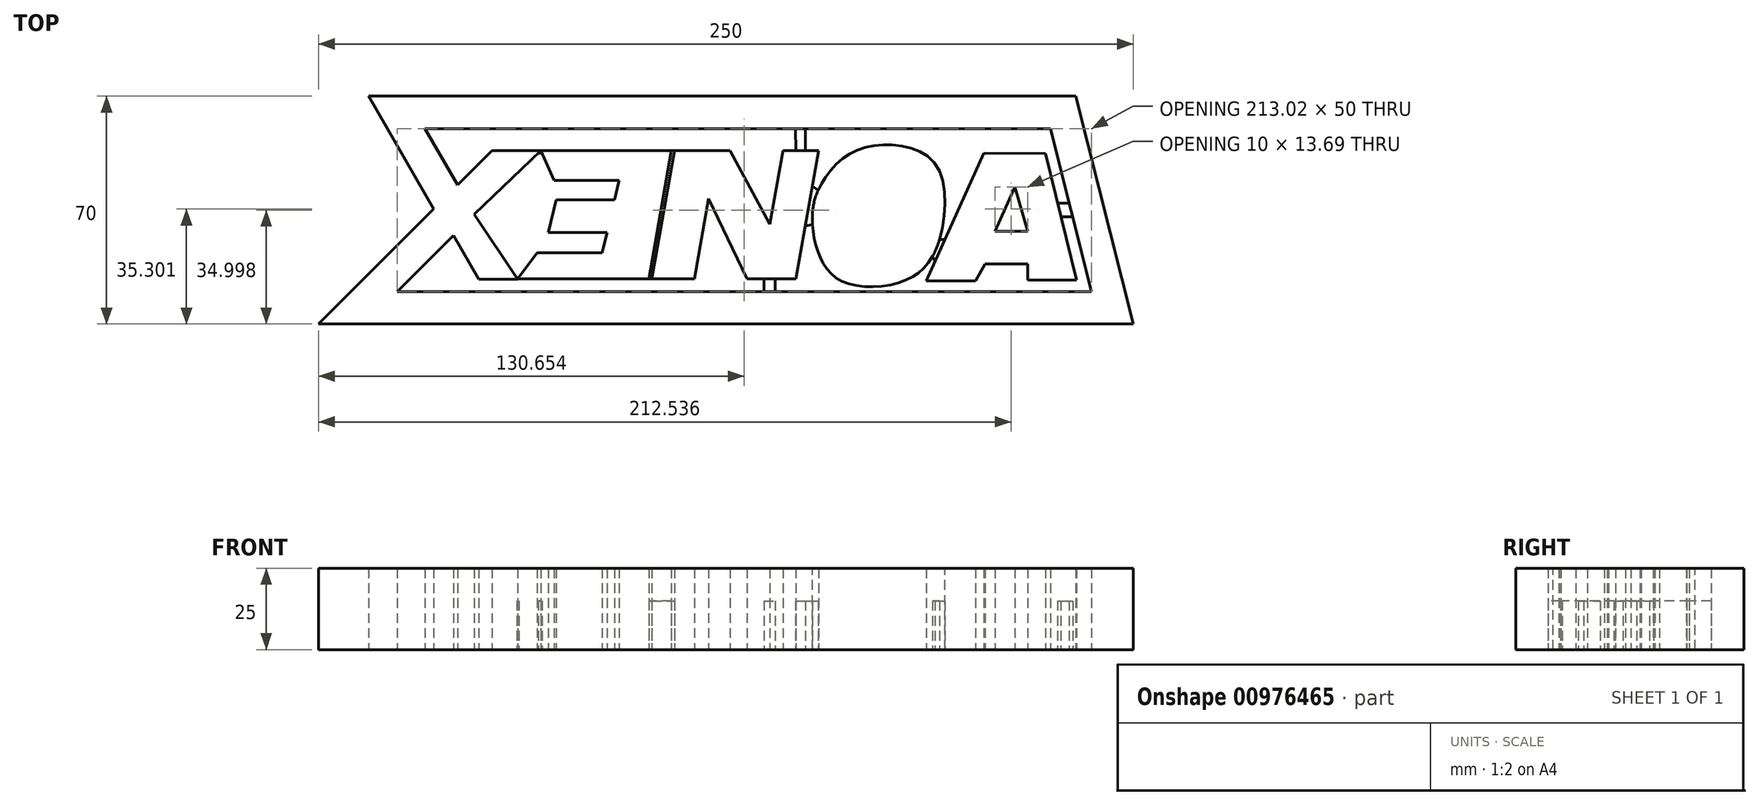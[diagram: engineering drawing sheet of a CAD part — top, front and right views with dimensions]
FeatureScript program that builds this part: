
annotation { "Feature Type Name" : "Feature", "Feature Type Description" : "" }
export const myFeature = defineFeature(function(context is Context, id is Id, definition is map)
    precondition{}
    {
        {
            var Q0;
            Q0=qCreatedBy(makeId("Top.planeOp"),FACE);
            var sketch = newSketch(context, id + "F0", { "sketchPlane" : qUnion([Q0])});
            skLineSegment(sketch, "E0", {"start": v(0, 0) * mm, "end": v(250, 0) * mm});
            skLineSegment(sketch, "E1", {"start": v(0, 0) * mm, "end": v(35.36, 35.36) * mm});
            skLineSegment(sketch, "E2", {"start": v(35.36, 35.36) * mm, "end": v(15.36, 70) * mm});
            skLineSegment(sketch, "E3", {"start": v(15.36, 70) * mm, "end": v(232.36, 70) * mm});
            skLineSegment(sketch, "E4", {"start": v(232.36, 70) * mm, "end": v(250, 0) * mm});
            skLineSegment(sketch, "E5.0", {"start": v(224.56, 60) * mm, "end": v(237.17, 10) * mm});
            skLineSegment(sketch, "E5.1", {"start": v(32.68, 60) * mm, "end": v(224.56, 60) * mm});
            skLineSegment(sketch, "E5.2", {"start": v(24.14, 10) * mm, "end": v(237.17, 10) * mm});
            skLineSegment(sketch, "E5.3", {"start": v(24.14, 10) * mm, "end": v(47.85, 33.71) * mm});
            skLineSegment(sketch, "E5.4", {"start": v(47.85, 33.71) * mm, "end": v(32.68, 60) * mm});
            skLineSegment(sketch, "E6", {"start": v(42.68, 42.68) * mm, "end": v(53.28, 53.28) * mm});
            skLineSegment(sketch, "E7", {"start": v(53.28, 53.28) * mm, "end": v(68.28, 53.28) * mm});
            skLineSegment(sketch, "E8", {"start": v(68.28, 53.28) * mm, "end": v(47.85, 33.71) * mm});
            skLineSegment(sketch, "E9", {"start": v(47.85, 33.71) * mm, "end": v(61.2, 13.76) * mm});
            skLineSegment(sketch, "E10", {"start": v(61.2, 13.76) * mm, "end": v(49.2, 13.76) * mm});
            skLineSegment(sketch, "E11", {"start": v(49.2, 13.76) * mm, "end": v(41.4, 27.26) * mm});
            skLineSegment(sketch, "E12", {"start": v(68.28, 53.28) * mm, "end": v(108.28, 53.28) * mm});
            skLineSegment(sketch, "E13", {"start": v(108.28, 53.28) * mm, "end": v(101.34, 13.9) * mm});
            skLineSegment(sketch, "E14", {"start": v(101.34, 13.9) * mm, "end": v(61.2, 13.9) * mm});
            skLineSegment(sketch, "E15", {"start": v(61.2, 13.9) * mm, "end": v(67.1, 21.96) * mm});
            skLineSegment(sketch, "E16", {"start": v(68.28, 53.28) * mm, "end": v(72.31, 44.13) * mm});
            skLineSegment(sketch, "E17", {"start": v(72.31, 44.13) * mm, "end": v(92.31, 44.13) * mm});
            skLineSegment(sketch, "E18", {"start": v(67.1, 21.96) * mm, "end": v(87.1, 21.96) * mm});
            skLineSegment(sketch, "E19", {"start": v(108.28, 53.28) * mm, "end": v(109.28, 53.28) * mm});
            skLineSegment(sketch, "E20", {"start": v(101.34, 13.9) * mm, "end": v(102.34, 13.9) * mm});
            skLineSegment(sketch, "E21", {"start": v(102.34, 13.9) * mm, "end": v(109.28, 53.28) * mm});
            skLineSegment(sketch, "E22", {"start": v(109.28, 53.28) * mm, "end": v(126.28, 53.28) * mm});
            skLineSegment(sketch, "E23", {"start": v(102.34, 13.9) * mm, "end": v(115.34, 13.9) * mm});
            skLineSegment(sketch, "E24", {"start": v(115.34, 13.9) * mm, "end": v(119.68, 38.51) * mm});
            skLineSegment(sketch, "E25", {"start": v(119.68, 38.51) * mm, "end": v(131.54, 13.92) * mm});
            skLineSegment(sketch, "E26", {"start": v(131.54, 13.92) * mm, "end": v(146.54, 13.92) * mm});
            skLineSegment(sketch, "E27", {"start": v(146.54, 13.92) * mm, "end": v(153.48, 53.31) * mm});
            skLineSegment(sketch, "E28", {"start": v(142.52, 53.31) * mm, "end": v(138.53, 30.66) * mm});
            skLineSegment(sketch, "E29", {"start": v(138.53, 30.66) * mm, "end": v(126.28, 53.28) * mm});
            skLineSegment(sketch, "E30", {"start": v(92.31, 44.13) * mm, "end": v(87.1, 21.96) * mm});
            skPoint(sketch, "E31", {"position": v(89.73, 33.13) * mm});
            skPoint(sketch, "E32", {"position": v(90.9, 38.13) * mm});
            skPoint(sketch, "E33", {"position": v(88.55, 28.13) * mm});
            skLineSegment(sketch, "E34", {"start": v(90.9, 38.13) * mm, "end": v(72.9, 38.13) * mm});
            skLineSegment(sketch, "E35", {"start": v(88.55, 28.13) * mm, "end": v(70.55, 28.13) * mm});
            skLineSegment(sketch, "E36", {"start": v(70.55, 28.13) * mm, "end": v(72.9, 38.13) * mm});
            skPoint(sketch, "E37", {"position": v(150, 33.62) * mm});
            skLineSegment(sketch, "E38", {"start": v(142.52, 53.31) * mm, "end": v(153.48, 53.31) * mm});
            skLineSegment(sketch, "E39", {"start": v(223.08, 52.32) * mm, "end": v(232.54, 13.45) * mm});
            skLineSegment(sketch, "E40", {"start": v(232.54, 13.45) * mm, "end": v(217.54, 13.45) * mm});
            skLineSegment(sketch, "E41", {"start": v(217.54, 13.45) * mm, "end": v(217.54, 18.45) * mm});
            skLineSegment(sketch, "E42", {"start": v(217.54, 18.45) * mm, "end": v(204.54, 18.45) * mm});
            skLineSegment(sketch, "E43", {"start": v(204.54, 18.45) * mm, "end": v(201.54, 13.26) * mm});
            skLineSegment(sketch, "E44", {"start": v(201.54, 13.26) * mm, "end": v(186.54, 13.26) * mm});
            skLineSegment(sketch, "E45", {"start": v(186.54, 13.26) * mm, "end": v(204.08, 52.51) * mm});
            skLineSegment(sketch, "E46", {"start": v(204.08, 52.51) * mm, "end": v(223.08, 52.32) * mm});
            skLineSegment(sketch, "E47", {"start": v(217.54, 18.45) * mm, "end": v(217.54, 28.45) * mm});
            skLineSegment(sketch, "E48", {"start": v(217.54, 28.45) * mm, "end": v(207.54, 28.45) * mm});
            skLineSegment(sketch, "E49", {"start": v(207.54, 28.45) * mm, "end": v(213.66, 42.15) * mm});
            skLineSegment(sketch, "E50", {"start": v(213.66, 42.15) * mm, "end": v(217.54, 28.45) * mm});
            skFitSpline(sketch, "E51", {"points": [v(151.53, 33.62) * mm, v(153.96, 42.44) * mm, v(162.22, 51.87) * mm, v(176.24, 55.02) * mm, v(189.9, 48.28) * mm, v(190.07, 24.56) * mm, v(179.83, 13.34) * mm, v(161.41, 12.8) * mm, v(153.5, 21.42) * mm, v(151.53, 33.62) * mm]});
            skFitSpline(sketch, "E52.0", {"points": [v(161.5, 32.03) * mm, v(161.5, 33.17) * mm, v(161.6, 34.1) * mm, v(161.72, 34.9) * mm, v(161.9, 35.62) * mm, v(162.1, 36.23) * mm, v(162.32, 36.76) * mm, v(162.51, 37.2) * mm, v(162.74, 37.66) * mm, v(163.1, 38.33) * mm, v(163.6, 39.18) * mm, v(164.29, 40.2) * mm, v(165.04, 41.16) * mm, v(165.83, 42.02) * mm, v(166.5, 42.63) * mm, v(167.02, 43.04) * mm, v(167.4, 43.32) * mm, v(167.76, 43.55) * mm, v(168.15, 43.77) * mm, v(168.57, 43.97) * mm, v(169.16, 44.23) * mm, v(169.98, 44.52) * mm, v(171.09, 44.8) * mm, v(172.32, 44.98) * mm, v(173.66, 45.08) * mm, v(174.73, 45.08) * mm, v(175.47, 45.05) * mm, v(175.97, 45.02) * mm, v(176.58, 44.96) * mm, v(177.28, 44.87) * mm, v(178.15, 44.72) * mm, v(179.13, 44.48) * mm, v(180.04, 44.14) * mm, v(180.66, 43.8) * mm, v(180.95, 43.58) * mm, v(181.1, 43.43) * mm, v(181.19, 43.33) * mm, v(181.25, 43.24) * mm, v(181.3, 43.16) * mm, v(181.36, 43.06) * mm, v(181.42, 42.92) * mm, v(181.52, 42.7) * mm, v(181.7, 42.18) * mm, v(181.98, 41.11) * mm, v(182.2, 39.44) * mm, v(182.28, 37.48) * mm, v(182.2, 35.37) * mm, v(181.95, 33.2) * mm, v(181.56, 31.09) * mm, v(181.07, 29.13) * mm, v(180.5, 27.45) * mm, v(179.93, 26.15) * mm, v(179.38, 25.18) * mm, v(178.87, 24.48) * mm, v(178.37, 23.95) * mm, v(177.83, 23.5) * mm, v(177.14, 23.07) * mm, v(176.21, 22.64) * mm, v(174.96, 22.2) * mm, v(173.46, 21.83) * mm, v(171.82, 21.57) * mm, v(170.14, 21.44) * mm, v(168.53, 21.45) * mm, v(167.32, 21.56) * mm, v(166.48, 21.7) * mm, v(165.94, 21.82) * mm, v(165.57, 21.92) * mm, v(165.33, 22) * mm, v(165.17, 22.06) * mm, v(165.05, 22.11) * mm, v(164.9, 22.18) * mm, v(164.74, 22.27) * mm, v(164.57, 22.37) * mm, v(164.38, 22.52) * mm, v(164.13, 22.75) * mm, v(163.8, 23.16) * mm, v(163.4, 23.77) * mm, v(163, 24.6) * mm, v(162.58, 25.68) * mm, v(162.21, 26.88) * mm, v(161.81, 28.59) * mm, v(161.57, 30.37) * mm, v(161.5, 32.03) * mm, v(161.5, 33.17) * mm, v(161.6, 34.1) * mm, v(161.5, 32.03) * mm]});
            skLineSegment(sketch, "E53", {"start": v(179.1, 44.47) * mm, "end": v(162.82, 25.07) * mm});
            skLineSegment(sketch, "E54", {"start": v(181.97, 41) * mm, "end": v(165.9, 21.83) * mm});
            skLineSegment(sketch, "E55", {"start": v(67.44, 52.48) * mm, "end": v(68.64, 52.48) * mm});
            skLineSegment(sketch, "E56", {"start": v(60.85, 14.28) * mm, "end": v(61.48, 14.28) * mm});
            skLineSegment(sketch, "E57", {"start": v(61.2, 13.76) * mm, "end": v(61.2, 13.9) * mm});
            skLineSegment(sketch, "E58", {"start": v(151.55, 42.38) * mm, "end": v(153.3, 41.08) * mm});
            skLineSegment(sketch, "E59", {"start": v(149.4, 30.13) * mm, "end": v(151.56, 30.5) * mm});
            skLineSegment(sketch, "E60", {"start": v(190.55, 26.02) * mm, "end": v(192.24, 26.02) * mm});
            skLineSegment(sketch, "E61", {"start": v(188.42, 20.85) * mm, "end": v(189.2, 19.2) * mm});
            skLineSegment(sketch, "E62", {"start": v(226.76, 37.18) * mm, "end": v(230.31, 37.18) * mm});
            skLineSegment(sketch, "E63", {"start": v(227.8, 32.89) * mm, "end": v(231.4, 32.89) * mm});
            skLineSegment(sketch, "E64", {"start": v(146.33, 60) * mm, "end": v(146.52, 53.31) * mm});
            skLineSegment(sketch, "E65", {"start": v(149.35, 60) * mm, "end": v(149.35, 53.31) * mm});
            skLineSegment(sketch, "E66", {"start": v(136.68, 13.92) * mm, "end": v(136.68, 10) * mm});
            skLineSegment(sketch, "E67", {"start": v(140.15, 13.92) * mm, "end": v(140.15, 10) * mm});
            skSolve(sketch);
        }
        {
            var Q0;
            Q0=makeQuery(id+"F0.imprint","IMPRINT",FACE,{"disambiguationData":[TD([[makeQuery(id+"F0.imprint","IMPRINT",EDGE,{"derivedFrom":sQuery(id+"F0.wireOp",EDGE,"E0")}),1.0]])]});
            var Q1;
            {var subQ2=sQuery(id+"F0.wireOp",EDGE,"E6");Q1=makeQuery(id+"F0.imprint","IMPRINT",FACE,{"disambiguationData":[TD([[makeQuery(id+"F0.imprint","IMPRINT",EDGE,{"derivedFrom":subQ2}),-1.0]])]});}
            var Q2;
            {var subQ0=sQuery(id+"F0.wireOp",EDGE,"E9");Q2=makeQuery(id+"F0.imprint","IMPRINT",FACE,{"disambiguationData":[TD([[makeQuery(id+"F0.imprint","IMPRINT",EDGE,{"derivedFrom":subQ0}),-1.0]])]});}
            var Q3;
            {var subQ0=sQuery(id+"F0.wireOp",EDGE,"E34");Q3=makeQuery(id+"F0.imprint","IMPRINT",FACE,{"disambiguationData":[TD([[makeQuery(id+"F0.imprint","IMPRINT",EDGE,{"derivedFrom":subQ0}),1.0]])]});}
            var Q4;
            Q4=makeQuery(id+"F0.imprint","IMPRINT",FACE,{"disambiguationData":[TD([[makeQuery(id+"F0.imprint","IMPRINT",EDGE,{"derivedFrom":sQuery(id+"F0.wireOp",EDGE,"E12")}),-1.0]])]});
            var Q5;
            Q5=makeQuery(id+"F0.imprint","IMPRINT",FACE,{"disambiguationData":[TD([[makeQuery(id+"F0.imprint","IMPRINT",EDGE,{"derivedFrom":sQuery(id+"F0.wireOp",EDGE,"E21")}),-1.0]])]});
            var Q6;
            Q6=makeQuery(id+"F0.imprint","IMPRINT",FACE,{"disambiguationData":[TD([[makeQuery(id+"F0.imprint","IMPRINT",EDGE,{"derivedFrom":sQuery(id+"F0.wireOp",EDGE,"E51")}),-1.0]])]});
            var Q7;
            {var subQ0=sQuery(id+"F0.wireOp",EDGE,"E53");Q7=makeQuery(id+"F0.imprint","IMPRINT",FACE,{"disambiguationData":[TD([[makeQuery(id+"F0.imprint","IMPRINT",EDGE,{"derivedFrom":subQ0}),1.0]])]});}
            var Q8;
            Q8=makeQuery(id+"F0.imprint","IMPRINT",FACE,{"disambiguationData":[TD([[makeQuery(id+"F0.imprint","IMPRINT",EDGE,{"derivedFrom":sQuery(id+"F0.wireOp",EDGE,"E39")}),-1.0]])]});
            var Q9;
            {var subQ0=sQuery(id+"F0.wireOp",EDGE,"JfNl9Xfk-aqaR-qNYz-ximk-0m5AAW0ROm31");Q9=makeQuery(id+"F0.imprint","IMPRINT",FACE,{"disambiguationData":[TD([[makeQuery(id+"F0.imprint","IMPRINT",EDGE,{"derivedFrom":subQ0}),-1.0]])]});}
            var Q10;
            {var subQ0=sQuery(id+"F0.wireOp",EDGE,"E15");var subQ1=sQuery(id+"F0.wireOp",EDGE,"E14");var subQ2=makeQuery(id+"F0.imprint","INTERSECT",VERTEX,{"derivedFrom":[subQ1,subQ0]});Q10=makeQuery(id+"F0.imprint","IMPRINT",FACE,{"disambiguationData":[TD([[makeQuery(id+"F0.imprint","IMPRINT",EDGE,{"disambiguationData":[TD([[subQ2,1.0]])],"derivedFrom":subQ1}),-1.0]])]});}
            var Q11;
            {var subQ3=sQuery(id+"F0.wireOp",EDGE,"eN30COPq-oqJq-rnKl-EqHf-OhdowSKKRAAw");Q11=makeQuery(id+"F0.imprint","IMPRINT",FACE,{"disambiguationData":[TD([[makeQuery(id+"F0.imprint","IMPRINT",EDGE,{"derivedFrom":subQ3}),1.0]])]});}
            var Q12;
            {var subQ0=sQuery(id+"F0.wireOp",EDGE,"imM2ijot-e2D8-q0Y7-5tzL-eRpiLB6fCpNz");Q12=makeQuery(id+"F0.imprint","IMPRINT",FACE,{"disambiguationData":[TD([[makeQuery(id+"F0.imprint","IMPRINT",EDGE,{"derivedFrom":subQ0}),-1.0]])]});}
            var Q13;
            {var subQ0=sQuery(id+"F0.wireOp",EDGE,"RDafbrLf-kzFO-E4ZM-40qh-3E63GRLbKq8Y");Q13=makeQuery(id+"F0.imprint","IMPRINT",FACE,{"disambiguationData":[TD([[makeQuery(id+"F0.imprint","IMPRINT",EDGE,{"derivedFrom":subQ0}),-1.0]])]});}
            var Q14;
            {var subQ0=sQuery(id+"F0.wireOp",EDGE,"6cAeuiRb-naha-nZBh-ziNz-JyJCdYFGemb1");Q14=makeQuery(id+"F0.imprint","IMPRINT",FACE,{"disambiguationData":[TD([[makeQuery(id+"F0.imprint","IMPRINT",EDGE,{"derivedFrom":subQ0}),-1.0]])]});}
            var Q15;
            {var subQ0=sQuery(id+"F0.wireOp",EDGE,"ylp7s7nb-VYOC-vkmB-fRLy-HwE1BUQnb8ae");Q15=makeQuery(id+"F0.imprint","IMPRINT",FACE,{"disambiguationData":[TD([[makeQuery(id+"F0.imprint","IMPRINT",EDGE,{"derivedFrom":subQ0}),-1.0]])]});}
            var Q16;
            {var subQ0=sQuery(id+"F0.wireOp",EDGE,"D8vqczcZ-tITf-OYWz-xtXg-1sGLX5qLOuWc");Q16=makeQuery(id+"F0.imprint","IMPRINT",FACE,{"disambiguationData":[TD([[makeQuery(id+"F0.imprint","IMPRINT",EDGE,{"derivedFrom":subQ0}),-1.0]])]});}
            extrude(context, id + "F1", {"entities" : qUnion([Q0, Q1, Q2, Q3, Q4, Q5, Q6, Q7, Q8, Q9, Q10, Q11, Q12, Q13, Q14, Q15, Q16]), "depth" : 25 * mm, "offsetDistance" : 25 * mm});
        }
        {
            var Q0;
            {var subQ0=sQuery(id+"F0.wireOp",EDGE,"E64");Q0=makeQuery(id+"F0.imprint","IMPRINT",FACE,{"disambiguationData":[TD([[makeQuery(id+"F0.imprint","IMPRINT",EDGE,{"derivedFrom":subQ0}),1.0]])]});}
            var Q1;
            {var subQ0=sQuery(id+"F0.wireOp",EDGE,"E66");Q1=makeQuery(id+"F0.imprint","IMPRINT",FACE,{"disambiguationData":[TD([[makeQuery(id+"F0.imprint","IMPRINT",EDGE,{"derivedFrom":subQ0}),1.0]])]});}
            var Q2;
            {var subQ0=sQuery(id+"F0.wireOp",EDGE,"E58");Q2=makeQuery(id+"F0.imprint","IMPRINT",FACE,{"disambiguationData":[TD([[makeQuery(id+"F0.imprint","IMPRINT",EDGE,{"derivedFrom":subQ0}),-1.0]])]});}
            var Q3;
            {var subQ0=sQuery(id+"F0.wireOp",EDGE,"E60");Q3=makeQuery(id+"F0.imprint","IMPRINT",FACE,{"disambiguationData":[TD([[makeQuery(id+"F0.imprint","IMPRINT",EDGE,{"derivedFrom":subQ0}),-1.0]])]});}
            var Q4;
            {var subQ0=sQuery(id+"F0.wireOp",EDGE,"E62");Q4=makeQuery(id+"F0.imprint","IMPRINT",FACE,{"disambiguationData":[TD([[makeQuery(id+"F0.imprint","IMPRINT",EDGE,{"derivedFrom":subQ0}),-1.0]])]});}
            var Q5;
            Q5=makeQuery(id+"F0.imprint","IMPRINT",FACE,{"disambiguationData":[TD([[makeQuery(id+"F0.imprint","IMPRINT",EDGE,{"derivedFrom":sQuery(id+"F0.wireOp",EDGE,"E13")}),1.0]])]});
            var Q6;
            {var subQ2=sQuery(id+"F0.wireOp",EDGE,"E56");Q6=makeQuery(id+"F0.imprint","IMPRINT",FACE,{"disambiguationData":[TD([[makeQuery(id+"F0.imprint","IMPRINT",EDGE,{"derivedFrom":subQ2}),-1.0]])]});}
            var Q7;
            {var subQ3=sQuery(id+"F0.wireOp",EDGE,"E55");Q7=makeQuery(id+"F0.imprint","IMPRINT",FACE,{"disambiguationData":[TD([[makeQuery(id+"F0.imprint","IMPRINT",EDGE,{"derivedFrom":subQ3}),1.0]])]});}
            extrude(context, id + "F2", {"entities" : qUnion([Q0, Q1, Q2, Q3, Q4, Q5, Q6, Q7]), "depth" : 15 * mm, "offsetDistance" : 25 * mm});
        }
    });
